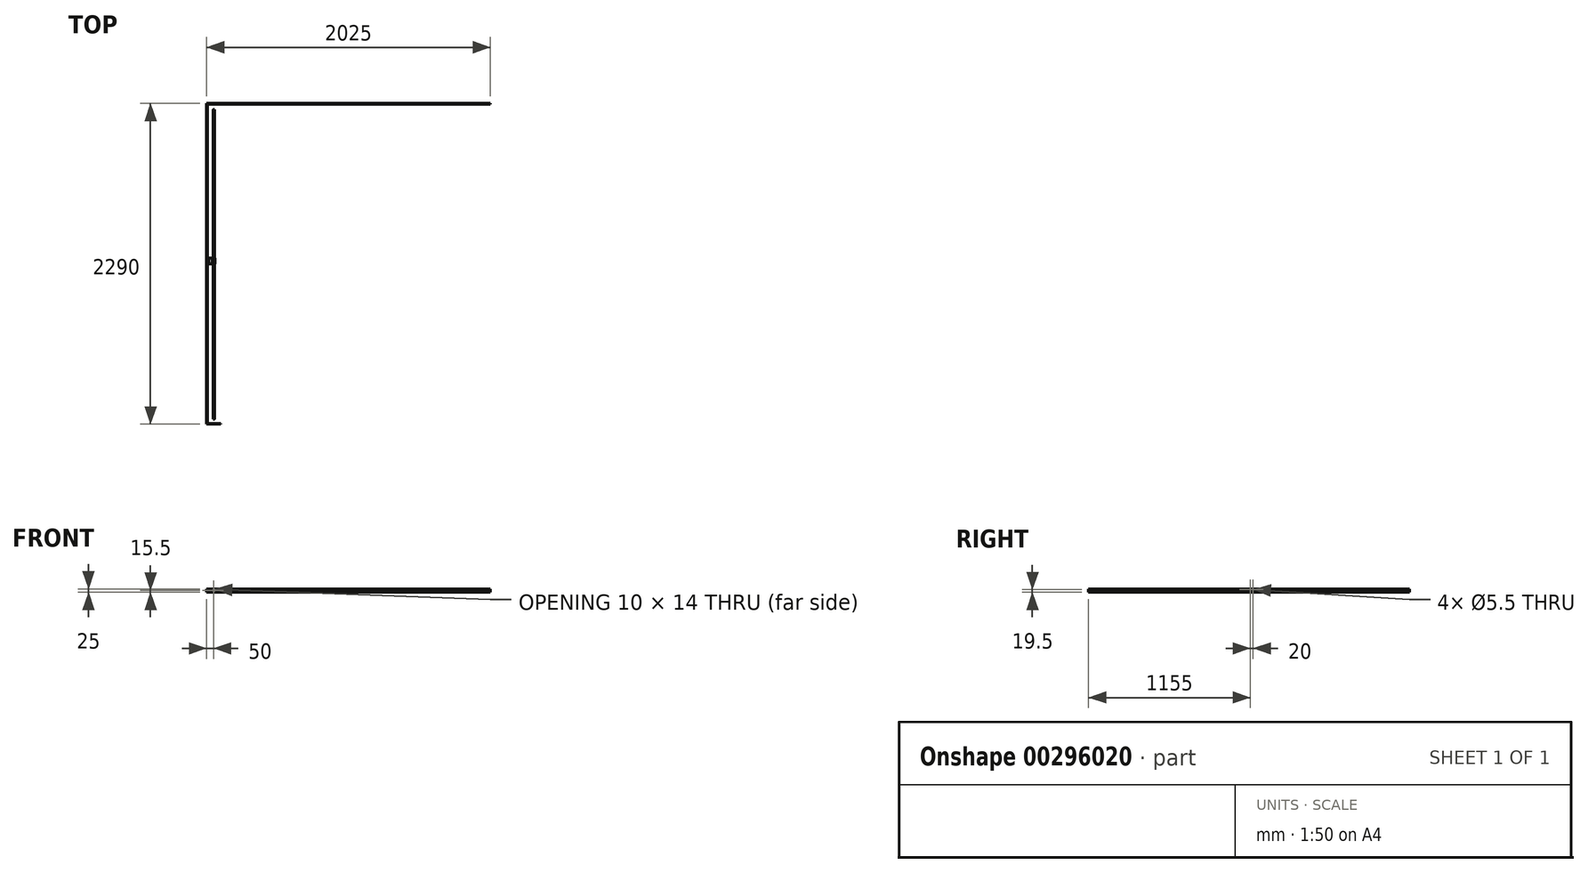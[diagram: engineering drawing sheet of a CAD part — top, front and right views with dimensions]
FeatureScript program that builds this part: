
annotation { "Feature Type Name" : "Feature", "Feature Type Description" : "" }
export const myFeature = defineFeature(function(context is Context, id is Id, definition is map)
    precondition{}
    {
        {
            var Q0;
            Q0=qCreatedBy(makeId("Right.planeOp"),FACE);
            var sketch = newSketch(context, id + "F0", { "sketchPlane" : qUnion([Q0])});
            skLineSegment(sketch, "E0.bottom", {"start": v(0, 0) * mm, "end": v(2280, 0) * mm});
            skLineSegment(sketch, "E0.top", {"start": v(0, 25) * mm, "end": v(2280, 25) * mm});
            skLineSegment(sketch, "E0.left", {"start": v(0, 0) * mm, "end": v(0, 25) * mm});
            skLineSegment(sketch, "E0.right", {"start": v(2280, 0) * mm, "end": v(2280, 25) * mm});
            skSolve(sketch);
        }
        {
            var Q0;
            Q0 = qSketchRegion(id + "F0", true);
            extrude(context, id + "F1", {"entities" : qUnion([Q0]), "depth" : 5 * mm, "offsetDistance" : 25 * mm});
        }
        {
            var Q0;
            Q0=makeQuery(id+"F1.opExtrude","SWEPT_FACE",FACE,{"disambiguationData":[OSD([sQuery(id+"F0.wireOp",EDGE,"E0.right")])]});
            var sketch = newSketch(context, id + "F2", { "sketchPlane" : qUnion([Q0])});
            skLineSegment(sketch, "E1.bottom", {"start": v(0, 25) * mm, "end": v(-2025, 25) * mm});
            skLineSegment(sketch, "E1.top", {"start": v(0, 0) * mm, "end": v(-2025, 0) * mm});
            skLineSegment(sketch, "E1.left", {"start": v(0, 25) * mm, "end": v(0, 0) * mm});
            skLineSegment(sketch, "E1.right", {"start": v(-2025, 25) * mm, "end": v(-2025, 0) * mm});
            skSolve(sketch);
        }
        {
            var Q0;
            Q0 = qSketchRegion(id + "F2", true);
            extrude(context, id + "F3", {"entities" : qUnion([Q0]), "operationType" : NewBodyOperationType.ADD, "depth" : 5 * mm, "offsetDistance" : 25 * mm});
        }
        {
            var Q0;
            Q0=makeQuery(id+"F1.opExtrude","SWEPT_FACE",FACE,{"disambiguationData":[OSD([sQuery(id+"F0.wireOp",EDGE,"E0.left")])]});
            var sketch = newSketch(context, id + "F4", { "sketchPlane" : qUnion([Q0])});
            skLineSegment(sketch, "E2.bottom", {"start": v(0, 25) * mm, "end": v(100, 25) * mm});
            skLineSegment(sketch, "E2.top", {"start": v(0, 0) * mm, "end": v(100, 0) * mm});
            skLineSegment(sketch, "E2.left", {"start": v(0, 25) * mm, "end": v(0, 0) * mm});
            skLineSegment(sketch, "E2.right", {"start": v(100, 25) * mm, "end": v(100, 0) * mm});
            skSolve(sketch);
        }
        {
            var Q0;
            Q0 = qSketchRegion(id + "F4", true);
            extrude(context, id + "F5", {"entities" : qUnion([Q0]), "operationType" : NewBodyOperationType.ADD, "depth" : 5 * mm, "offsetDistance" : 25 * mm});
        }
        {
            var Q0;
            Q0=makeQuery(id+"F1.opExtrude","CAP_FACE",FACE,{"disambiguationData":[OSD([sQuery(id+"F0.wireOp",EDGE,"E0.bottom"),sQuery(id+"F0.wireOp",EDGE,"E0.top"),sQuery(id+"F0.wireOp",EDGE,"E0.left"),sQuery(id+"F0.wireOp",EDGE,"E0.right")])],"isStart":false});
            var sketch = newSketch(context, id + "F6", { "sketchPlane" : qUnion([Q0])});
            skLineSegment(sketch, "E3.bottom", {"start": v(1140, 25) * mm, "end": v(1180, 25) * mm});
            skLineSegment(sketch, "E3.top", {"start": v(1140, 2.5) * mm, "end": v(1180, 2.5) * mm});
            skLineSegment(sketch, "E3.left", {"start": v(1140, 25) * mm, "end": v(1140, 2.5) * mm});
            skLineSegment(sketch, "E3.right", {"start": v(1180, 25) * mm, "end": v(1180, 2.5) * mm});
            skSolve(sketch);
        }
        {
            var Q0;
            Q0 = qSketchRegion(id + "F6", true);
            extrude(context, id + "F7", {"entities" : qUnion([Q0]), "depth" : 10 * mm, "offsetDistance" : 25 * mm});
        }
        {
            var Q0;
            Q0=makeQuery(id+"F7.opExtrude","SWEPT_EDGE",EDGE,{"disambiguationData":[OSD([sQuery(id+"F0.wireOp",EDGE,"E0.top"),sQuery(id+"F6.wireOp",EDGE,"E3.bottom"),sQuery(id+"F6.wireOp",EDGE,"E3.left")])]});
            var Q1;
            Q1=makeQuery(id+"F7.opExtrude","SWEPT_EDGE",EDGE,{"disambiguationData":[OSD([sQuery(id+"F0.wireOp",EDGE,"E0.top"),sQuery(id+"F6.wireOp",EDGE,"E3.bottom"),sQuery(id+"F6.wireOp",EDGE,"E3.right")])]});
            chamfer(context, id + "F8", {"entities" : qUnion([Q0, Q1]), "width" : 5 * mm, "tangentPropagation" : true});
        }
        {
            var Q0;
            Q0=makeQuery(id+"F7.opExtrude","CAP_FACE",FACE,{"disambiguationData":[OSD([sQuery(id+"F6.wireOp",EDGE,"E3.bottom"),sQuery(id+"F6.wireOp",EDGE,"E3.top"),sQuery(id+"F6.wireOp",EDGE,"E3.left"),sQuery(id+"F6.wireOp",EDGE,"E3.right")])],"isStart":false});
            var sketch = newSketch(context, id + "F9", { "sketchPlane" : qUnion([Q0])});
            skLineSegment(sketch, "E4.bottom", {"start": v(1140, 2.5) * mm, "end": v(1180, 2.5) * mm});
            skLineSegment(sketch, "E4.top", {"start": v(1140, 12.5) * mm, "end": v(1180, 12.5) * mm});
            skLineSegment(sketch, "E4.left", {"start": v(1140, 2.5) * mm, "end": v(1140, 12.5) * mm});
            skLineSegment(sketch, "E4.right", {"start": v(1180, 2.5) * mm, "end": v(1180, 12.5) * mm});
            skSolve(sketch);
        }
        {
            var Q0;
            Q0 = qSketchRegion(id + "F9", true);
            extrude(context, id + "F10", {"entities" : qUnion([Q0]), "operationType" : NewBodyOperationType.ADD, "depth" : 45 * mm, "offsetDistance" : 25 * mm});
        }
        {
            var Q0;
            Q0=makeQuery(id+"F10.boolean.opBoolean","MERGE",FACE,{"derivedFrom":[makeQuery(id+"F7.opExtrude","SWEPT_FACE",FACE,{"disambiguationData":[OSD([sQuery(id+"F6.wireOp",EDGE,"E3.left")])]}),makeQuery(id+"F10.opExtrude","SWEPT_FACE",FACE,{"disambiguationData":[OSD([sQuery(id+"F9.wireOp",EDGE,"E4.left")])]})]});
            var sketch = newSketch(context, id + "F11", { "sketchPlane" : qUnion([Q0])});
            skLineSegment(sketch, "E5.bottom", {"start": v(60, 12.5) * mm, "end": v(40, 12.5) * mm});
            skLineSegment(sketch, "E5.top", {"start": v(60, 22.5) * mm, "end": v(40, 22.5) * mm});
            skLineSegment(sketch, "E5.left", {"start": v(60, 12.5) * mm, "end": v(60, 22.5) * mm});
            skLineSegment(sketch, "E5.right", {"start": v(40, 12.5) * mm, "end": v(40, 22.5) * mm});
            skSolve(sketch);
        }
        {
            var Q0;
            Q0 = qSketchRegion(id + "F11", true);
            var Q1;
            Q1=makeQuery(id+"F10.opExtrude","CAP_VERTEX",VERTEX,{"disambiguationData":[OSD([sQuery(id+"F6.wireOp",EDGE,"E3.right"),sQuery(id+"F9.wireOp",EDGE,"E4.top"),sQuery(id+"F9.wireOp",EDGE,"E4.right")])],"isStart":false});
            extrude(context, id + "F12", {"entities" : qUnion([Q0]), "operationType" : NewBodyOperationType.ADD, "endBound" : BoundingType.UP_TO_VERTEX, "oppositeDirection" : true, "depth" : 25 * mm, "endBoundEntityVertex" : qUnion([Q1]), "offsetDistance" : 25 * mm});
        }
        {
            var Q0;
            Q0=makeQuery(id+"F12.boolean.opBoolean","MERGE",FACE,{"derivedFrom":[makeQuery(id+"F10.boolean.opBoolean","MERGE",FACE,{"derivedFrom":[makeQuery(id+"F7.opExtrude","SWEPT_FACE",FACE,{"disambiguationData":[OSD([sQuery(id+"F6.wireOp",EDGE,"E3.left")])]}),makeQuery(id+"F10.opExtrude","SWEPT_FACE",FACE,{"disambiguationData":[OSD([sQuery(id+"F9.wireOp",EDGE,"E4.left")])]})]}),makeQuery(id+"F12.opExtrude","CAP_FACE",FACE,{"disambiguationData":[OSD([sQuery(id+"F11.wireOp",EDGE,"E5.bottom"),sQuery(id+"F11.wireOp",EDGE,"E5.top"),sQuery(id+"F11.wireOp",EDGE,"E5.left"),sQuery(id+"F11.wireOp",EDGE,"E5.right")])],"isStart":true})]});
            var sketch = newSketch(context, id + "F13", { "sketchPlane" : qUnion([Q0])});
            skArc(sketch, "E6", {"start": v(45, 13.5) * mm, "mid": v(50, 8.5) * mm, "end": v(55, 13.5) * mm});
            skPoint(sketch, "E6.centerSnap0", {"position": v(50, 22.5) * mm});
            skLineSegment(sketch, "E7", {"start": v(45, 13.5) * mm, "end": v(45, 22.5) * mm});
            skLineSegment(sketch, "E8", {"start": v(55, 13.5) * mm, "end": v(55, 22.5) * mm});
            skLineSegment(sketch, "E9", {"start": v(45, 22.5) * mm, "end": v(55, 22.5) * mm});
            skSolve(sketch);
        }
        {
            var Q0;
            Q0 = qSketchRegion(id + "F13", true);
            extrude(context, id + "F14", {"entities" : qUnion([Q0]), "operationType" : NewBodyOperationType.REMOVE, "endBound" : BoundingType.THROUGH_ALL, "oppositeDirection" : true, "depth" : 25 * mm, "offsetDistance" : 25 * mm});
        }
        {
            var Q0;
            Q0=makeQuery(id+"F12.opExtrude","SWEPT_EDGE",EDGE,{"disambiguationData":[OSD([sQuery(id+"F11.wireOp",EDGE,"E5.top"),sQuery(id+"F11.wireOp",EDGE,"E5.left")])]});
            var Q1;
            Q1=makeQuery(id+"F12.opExtrude","SWEPT_EDGE",EDGE,{"disambiguationData":[OSD([sQuery(id+"F11.wireOp",EDGE,"E5.top"),sQuery(id+"F11.wireOp",EDGE,"E5.right")])]});
            var Q2;
            Q2=makeQuery(id+"F12.opExtrude","SWEPT_EDGE",EDGE,{"disambiguationData":[OSD([sQuery(id+"F6.wireOp",EDGE,"E3.left"),sQuery(id+"F9.wireOp",EDGE,"E4.top"),sQuery(id+"F9.wireOp",EDGE,"E4.left"),sQuery(id+"F11.wireOp",EDGE,"E5.bottom"),sQuery(id+"F11.wireOp",EDGE,"E5.right")])]});
            fillet(context, id + "F15", {"entities" : qUnion([Q0, Q1, Q2]), "radius" : 4.5 * mm, "tangentPropagation" : true, "allowEdgeOverflow" : false});
        }
        {
            var Q0;
            Q0=makeQuery(id+"F10.opExtrude","CAP_EDGE",EDGE,{"disambiguationData":[OSD([sQuery(id+"F9.wireOp",EDGE,"E4.bottom")])],"isStart":false});
            fillet(context, id + "F16", {"entities" : qUnion([Q0]), "radius" : 10 * mm, "tangentPropagation" : true, "allowEdgeOverflow" : false});
        }
        {
            var Q0;
            Q0=makeQuery(id+"F7.opExtrude","CAP_FACE",FACE,{"disambiguationData":[OSD([sQuery(id+"F6.wireOp",EDGE,"E3.bottom"),sQuery(id+"F6.wireOp",EDGE,"E3.top"),sQuery(id+"F6.wireOp",EDGE,"E3.left"),sQuery(id+"F6.wireOp",EDGE,"E3.right")])],"isStart":false});
            var sketch = newSketch(context, id + "F17", { "sketchPlane" : qUnion([Q0])});
            skCircle(sketch, "E10", {"center": v(1150, 19.5) * mm, "radius": 2.75 * mm});
            skCircle(sketch, "E11", {"center": v(1170, 19.5) * mm, "radius": 2.75 * mm});
            skSolve(sketch);
        }
        {
            var Q0;
            Q0 = qSketchRegion(id + "F17", true);
            extrude(context, id + "F18", {"entities" : qUnion([Q0]), "operationType" : NewBodyOperationType.REMOVE, "endBound" : BoundingType.THROUGH_ALL, "oppositeDirection" : true, "depth" : 25 * mm, "offsetDistance" : 25 * mm});
        }
        {
            var Q0;
            Q0=makeQuery(id+"F12.boolean.opBoolean","MERGE",FACE,{"derivedFrom":[makeQuery(id+"F10.boolean.opBoolean","MERGE",FACE,{"derivedFrom":[makeQuery(id+"F7.opExtrude","SWEPT_FACE",FACE,{"disambiguationData":[OSD([sQuery(id+"F6.wireOp",EDGE,"E3.right")])]}),makeQuery(id+"F10.opExtrude","SWEPT_FACE",FACE,{"disambiguationData":[OSD([sQuery(id+"F9.wireOp",EDGE,"E4.right")])]})]}),makeQuery(id+"F12.opExtrude","CAP_FACE",FACE,{"disambiguationData":[OSD([sQuery(id+"F11.wireOp",EDGE,"E5.bottom"),sQuery(id+"F11.wireOp",EDGE,"E5.top"),sQuery(id+"F11.wireOp",EDGE,"E5.left"),sQuery(id+"F11.wireOp",EDGE,"E5.right")])],"isStart":false})]});
            var sketch = newSketch(context, id + "F19", { "sketchPlane" : qUnion([Q0])});
            skCircle(sketch, "E12", {"center": v(-50, 13.5) * mm, "radius": 5 * mm});
            skSolve(sketch);
        }
        {
            var Q0;
            Q0 = qSketchRegion(id + "F19", true);
            extrude(context, id + "F20", {"entities" : qUnion([Q0]), "operationType" : NewBodyOperationType.ADD, "depth" : 1060 * mm, "offsetDistance" : 25 * mm, "hasSecondDirection" : true, "secondDirectionOppositeDirection" : true, "secondDirectionDepth" : 1150 * mm});
        }
    });
